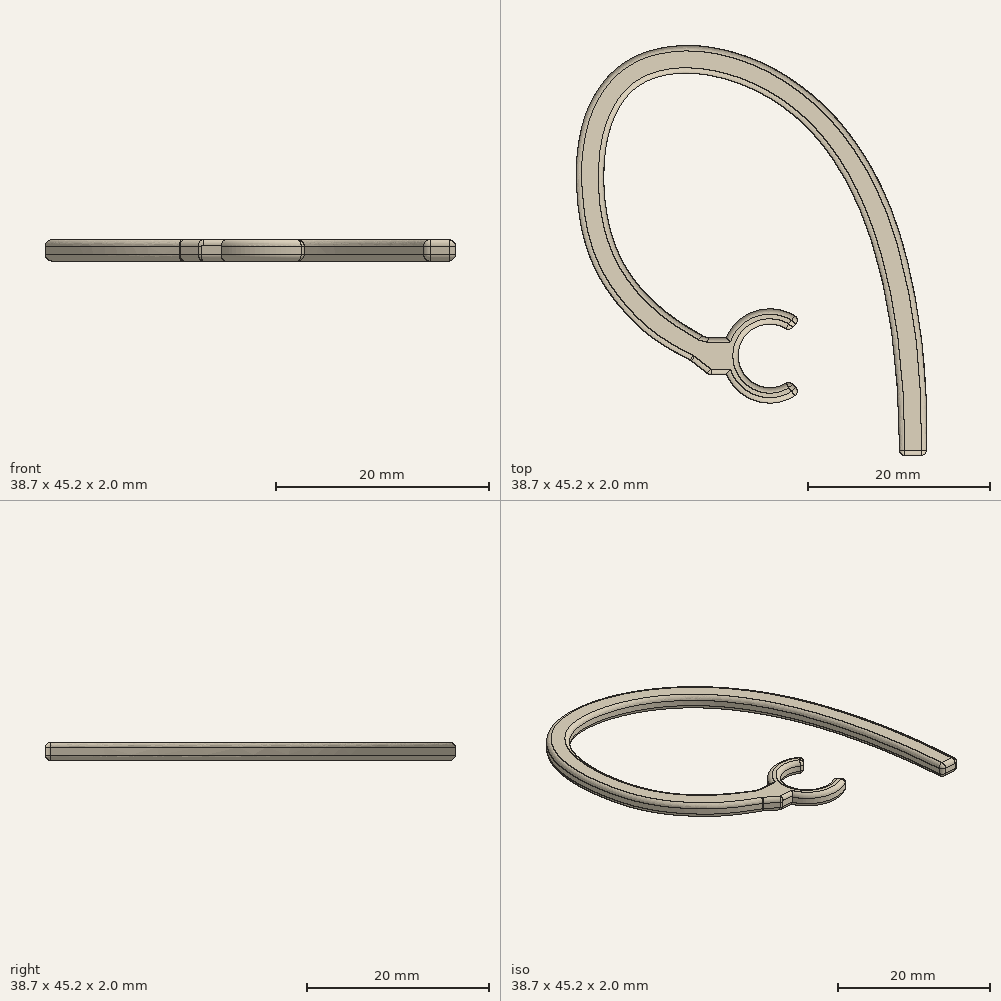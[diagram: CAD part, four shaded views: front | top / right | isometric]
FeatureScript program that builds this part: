
annotation { "Feature Type Name" : "Feature", "Feature Type Description" : "" }
export const myFeature = defineFeature(function(context is Context, id is Id, definition is map)
    precondition{}
    {
        {
            var Q0;
            Q0=qCreatedBy(makeId("Top.planeOp"),FACE);
            var sketch = newSketch(context, id + "F0", { "sketchPlane" : qUnion([Q0])});
            skArc(sketch, "E0", {"start": v(0, 5.5) * mm, "mid": v(-5.67, 2.75) * mm, "end": v(0, 0) * mm});
            skArc(sketch, "E1", {"start": v(1.16, 6.75) * mm, "mid": v(-7.37, 2.75) * mm, "end": v(1.16, -1.25) * mm});
            skLineSegment(sketch, "E2", {"start": v(1.16, 6.75) * mm, "end": v(0, 5.5) * mm});
            skLineSegment(sketch, "E3", {"start": v(0, 0) * mm, "end": v(1.16, -1.25) * mm});
            skLineSegment(sketch, "E4", {"start": v(-6.97, 4.75) * mm, "end": v(-8.97, 4.75) * mm});
            skLineSegment(sketch, "E5", {"start": v(-8.97, 4.75) * mm, "end": v(-8.97, 0.75) * mm});
            skLineSegment(sketch, "E6", {"start": v(-8.97, 0.75) * mm, "end": v(-6.97, 0.75) * mm});
            skFitSpline(sketch, "E7", {"points": [v(-9.45, 4.88) * mm, v(-20.37, 19.85) * mm, v(-16.56, 32.57) * mm, v(0, 29.69) * mm, v(12.13, -8.23) * mm], "startDerivative": vector(-99.13, 53.41) * mm, "endDerivative": vector(0, -156.61) * mm});
            skFitSpline(sketch, "E8.0", {"points": [v(-10.87, 2.24) * mm, v(-13.1, 3.45) * mm, v(-15.94, 5.4) * mm, v(-18.82, 8.31) * mm, v(-20.52, 10.66) * mm, v(-21.8, 13.12) * mm, v(-22.68, 15.65) * mm, v(-23.14, 17.8) * mm, v(-23.36, 19.52) * mm, v(-23.5, 21.26) * mm, v(-23.54, 23.48) * mm, v(-23.3, 26.15) * mm, v(-22.71, 28.76) * mm, v(-21.87, 30.84) * mm, v(-20.94, 32.4) * mm, v(-20.09, 33.48) * mm, v(-19.24, 34.3) * mm, v(-18.5, 34.9) * mm, v(-17.69, 35.43) * mm, v(-16.62, 35.98) * mm, v(-15.28, 36.45) * mm, v(-13.9, 36.77) * mm, v(-12, 36.99) * mm, v(-9.57, 36.92) * mm, v(-6.62, 36.37) * mm, v(-3.68, 35.37) * mm, v(-1.3, 34.19) * mm, v(0.53, 33.04) * mm, v(1.86, 32.07) * mm, v(3.12, 31) * mm, v(4.71, 29.46) * mm, v(6.53, 27.31) * mm, v(9.06, 23.46) * mm, v(11.58, 17.92) * mm, v(13.66, 10.2) * mm, v(14.87, 1.52) * mm, v(15.13, -4.89) * mm, v(15.13, -8.23) * mm]});
            skLineSegment(sketch, "E9", {"start": v(-9.45, 4.88) * mm, "end": v(-10.87, 2.24) * mm});
            skLineSegment(sketch, "E10", {"start": v(12.13, -8.23) * mm, "end": v(15.13, -8.23) * mm});
            skLineSegment(sketch, "E11", {"start": v(-9.45, 4.88) * mm, "end": v(-8.97, 4.75) * mm});
            skLineSegment(sketch, "E12", {"start": v(-10.87, 2.24) * mm, "end": v(-8.97, 0.75) * mm});
            skSolve(sketch);
        }
        {
            var Q0;
            Q0=makeQuery(id+"F0.imprint","IMPRINT",FACE,{"disambiguationData":[TD([[makeQuery(id+"F0.imprint","IMPRINT",EDGE,{"derivedFrom":sQuery(id+"F0.wireOp",EDGE,"E7")}),1.0]])]});
            var Q1;
            Q1=makeQuery(id+"F0.imprint","IMPRINT",FACE,{"disambiguationData":[TD([[makeQuery(id+"F0.imprint","IMPRINT",EDGE,{"derivedFrom":sQuery(id+"F0.wireOp",EDGE,"E5")}),-1.0]])]});
            extrude(context, id + "F1", {"entities" : qUnion([Q0, Q1]), "depth" : 2 * mm, "offsetDistance" : 25 * mm});
        }
        {
            var Q0;
            Q0=makeQuery(id+"F1.opExtrude","CAP_EDGE",EDGE,{"disambiguationData":[OSD([sQuery(id+"F0.wireOp",EDGE,"E7")])],"isStart":false});
            var Q1;
            Q1=makeQuery(id+"F1.opExtrude","CAP_EDGE",EDGE,{"disambiguationData":[OSD([sQuery(id+"F0.wireOp",EDGE,"E7")])],"isStart":true});
            var Q2;
            Q2=makeQuery(id+"F1.opExtrude","SWEPT_EDGE",EDGE,{"disambiguationData":[OSD([sQuery(id+"F0.wireOp",EDGE,"E8.0"),sQuery(id+"F0.wireOp",EDGE,"E9"),sQuery(id+"F0.wireOp",EDGE,"E12")])]});
            fillet(context, id + "F2", {"entities" : qUnion([Q0, Q1, Q2]), "radius" : 0.6 * mm, "tangentPropagation" : true, "allowEdgeOverflow" : false});
        }
        {
            var Q0;
            Q0=qCreatedBy(makeId("Top.planeOp"),FACE);
            var sketch = newSketch(context, id + "F3", { "sketchPlane" : qUnion([Q0])});
            skArc(sketch, "E13", {"start": v(0, 5.5) * mm, "mid": v(-5.67, 2.75) * mm, "end": v(0, 0) * mm});
            skArc(sketch, "E14", {"start": v(1.16, 6.75) * mm, "mid": v(-7.37, 2.75) * mm, "end": v(1.16, -1.25) * mm});
            skLineSegment(sketch, "E15", {"start": v(1.16, 6.75) * mm, "end": v(0, 5.5) * mm});
            skLineSegment(sketch, "E16", {"start": v(0, 0) * mm, "end": v(1.16, -1.25) * mm});
            skLineSegment(sketch, "E17", {"start": v(-6.97, 4.75) * mm, "end": v(-8.97, 4.75) * mm});
            skLineSegment(sketch, "E18", {"start": v(-8.97, 4.75) * mm, "end": v(-8.97, 0.75) * mm});
            skLineSegment(sketch, "E19", {"start": v(-8.97, 0.75) * mm, "end": v(-6.97, 0.75) * mm});
            skSolve(sketch);
        }
        {
            var Q0;
            Q0 = qSketchRegion(id + "F3", true);
            extrude(context, id + "F4", {"entities" : qUnion([Q0]), "operationType" : NewBodyOperationType.ADD, "depth" : 2 * mm, "offsetDistance" : 25 * mm});
        }
        {
            var Q0;
            {var subQ0=sQuery(id+"F3.wireOp",EDGE,"E14");Q0=makeQuery(id+"F4.opExtrude","CAP_EDGE",EDGE,{"disambiguationData":[OSD([subQ0]),TDD([makeQuery(id+"F3.imprint","IMPRINT",EDGE,{"disambiguationData":[TD([[makeQuery(id+"F3.imprint","INTERSECT",VERTEX,{"derivedFrom":[subQ0,sQuery(id+"F3.wireOp",EDGE,"E15")]}),-1.0]])],"derivedFrom":subQ0})])],"isStart":false});}
            var Q1;
            {var subQ0=sQuery(id+"F3.wireOp",EDGE,"E14");Q1=makeQuery(id+"F4.opExtrude","CAP_EDGE",EDGE,{"disambiguationData":[OSD([subQ0]),TDD([makeQuery(id+"F3.imprint","IMPRINT",EDGE,{"disambiguationData":[TD([[makeQuery(id+"F3.imprint","INTERSECT",VERTEX,{"derivedFrom":[subQ0,sQuery(id+"F3.wireOp",EDGE,"E16")]}),1.0]])],"derivedFrom":subQ0})])],"isStart":false});}
            var Q2;
            Q2=makeQuery(id+"F4.opExtrude","CAP_EDGE",EDGE,{"disambiguationData":[OSD([sQuery(id+"F3.wireOp",EDGE,"E13")])],"isStart":false});
            var Q3;
            Q3=makeQuery(id+"F4.opExtrude","SWEPT_FACE",FACE,{"disambiguationData":[OSD([sQuery(id+"F3.wireOp",EDGE,"E15")])]});
            var Q4;
            Q4=makeQuery(id+"F4.opExtrude","SWEPT_FACE",FACE,{"disambiguationData":[OSD([sQuery(id+"F3.wireOp",EDGE,"E16")])]});
            var Q5;
            Q5=makeQuery(id+"F4.boolean.opBoolean","MERGE",FACE,{"derivedFrom":[makeQuery(id+"F1.opExtrude","CAP_FACE",FACE,{"disambiguationData":[OSD([sQuery(id+"F0.wireOp",EDGE,"E5"),sQuery(id+"F0.wireOp",EDGE,"E7"),sQuery(id+"F0.wireOp",EDGE,"E8.0"),sQuery(id+"F0.wireOp",EDGE,"E10"),sQuery(id+"F0.wireOp",EDGE,"E11"),sQuery(id+"F0.wireOp",EDGE,"E12")])],"isStart":true}),makeQuery(id+"F4.opExtrude","CAP_FACE",FACE,{"disambiguationData":[OSD([sQuery(id+"F3.wireOp",EDGE,"E13"),sQuery(id+"F3.wireOp",EDGE,"E14"),sQuery(id+"F3.wireOp",EDGE,"E15"),sQuery(id+"F3.wireOp",EDGE,"E16"),sQuery(id+"F3.wireOp",EDGE,"E17"),sQuery(id+"F3.wireOp",EDGE,"E18"),sQuery(id+"F3.wireOp",EDGE,"E19")])],"isStart":true})]});
            var Q6;
            Q6=makeQuery(id+"F1.opExtrude","SWEPT_EDGE",EDGE,{"disambiguationData":[OSD([sQuery(id+"F0.wireOp",EDGE,"E8.0"),sQuery(id+"F0.wireOp",EDGE,"E10")])]});
            var Q7;
            Q7=makeQuery(id+"F1.opExtrude","CAP_EDGE",EDGE,{"disambiguationData":[OSD([sQuery(id+"F0.wireOp",EDGE,"E8.0")])],"isStart":false});
            fillet(context, id + "F5", {"entities" : qUnion([Q0, Q1, Q2, Q3, Q4, Q5, Q6, Q7]), "radius" : 0.6 * mm, "tangentPropagation" : true, "allowEdgeOverflow" : false});
        }
        {
            var Q0;
            Q0=makeQuery(id+"F4.opExtrude","CAP_EDGE",EDGE,{"disambiguationData":[OSD([sQuery(id+"F3.wireOp",EDGE,"E17")])],"isStart":false});
            var Q1;
            Q1=makeQuery(id+"F4.opExtrude","CAP_EDGE",EDGE,{"disambiguationData":[OSD([sQuery(id+"F3.wireOp",EDGE,"E19")])],"isStart":false});
            fillet(context, id + "F6", {"entities" : qUnion([Q0, Q1]), "radius" : 0.5 * mm, "tangentPropagation" : true, "allowEdgeOverflow" : false});
        }
        {
            var Q0;
            Q0=makeQuery(id+"F1.opExtrude","CAP_EDGE",EDGE,{"disambiguationData":[OSD([sQuery(id+"F0.wireOp",EDGE,"E11")])],"isStart":false});
            fillet(context, id + "F7", {"entities" : qUnion([Q0]), "radius" : 0.5 * mm, "tangentPropagation" : true, "allowEdgeOverflow" : false});
        }
    });
